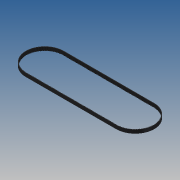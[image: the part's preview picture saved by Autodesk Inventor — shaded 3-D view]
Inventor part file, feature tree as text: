
AUTODESK INVENTOR PART (.ipt)
format: ipt  version: 2013 (Build 170138000, 138)  size: 629,248 bytes
history: native  units: mm
features: sketch x5, extrude x4, pattern_linear x1
ambient origin geometry x8: Origin, YZ Plane, XZ Plane, XY Plane, X Axis, Y Axis, Z Axis, Center Point
bodies: Solid1 (feature_tree)
feature tree (10):
  extrude  "Extrusion1"  Depth=31.830989mm
  extrude  "Extrusion2"  TaperAngle=180.0deg  [1 undecoded]
  extrude  "Extrusion4"  Depth=0.375mm
  sketch  "Sketch8"  dims[d15=6.0mm d16=0.0mm d17=6.0mm d18=0.0mm d19=2500.0mm]
  extrude  "Extrusion5"  Depth=0.629mm
  pattern_linear  "Rectangular Pattern1"  Spacing1=6.0mm  [1 undecoded]
  sketch  "Sketch1"  dims[d0=31.830989mm d2=31.830989mm]
  sketch  "Sketch2"  dims[d3=153.0mm d4=180.0deg]
  sketch  "Sketch5"  dims[d5=6.0mm d6=0.0mm d7=0.375mm]
  sketch  "Sketch7"  dims[d8=6.0mm d9=0.0mm d14=0.629mm]
note: 2 required parameter values undecoded (feature->parameter linkage not recoverable at this tier; creation-order binding heuristic only, values carry confidence <= 0.55)
